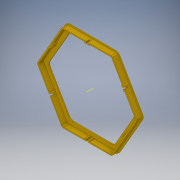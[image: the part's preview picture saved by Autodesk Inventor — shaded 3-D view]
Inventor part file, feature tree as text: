
AUTODESK INVENTOR PART (.ipt)
format: ipt  version: 2019 (Build 230136000, 136)  size: 541,696 bytes
history: native  units: mm
features: extrude x5, sketch x5, projected_geometry x3, fillet x2, other x1, pattern_circular x1
ambient origin geometry x8: Origin, YZ Plane, XZ Plane, XY Plane, X Axis, Y Axis, Z Axis, Center Point
bodies: Solid1 (feature_tree)
feature tree (17):
  extrude  "Extrusion1"  Depth=2.0mm
  extrude  "Extrusion5"  Depth=2.0mm
  extrude  "Extrusion6"  Depth=10.0mm
  fillet  "Fillet1"  [1 undecoded]
  fillet  "Fillet2"  Radius=8.0mm
  extrude  "Extrusion7"  TaperAngle=0.0deg  [1 undecoded]
  extrude  "Extrusion8"  Depth=4.0mm
  other  "Work Axis2"
  pattern_circular  "Circular Pattern1"  [2 undecoded]
  sketch  "Sketch1"  dims[d0=175.0mm d1=2.0mm]
  sketch  "Sketch5"  dims[d2=0.0mm d15=2.0mm]
  projected_geometry  "Projected Loop4"
  sketch  "Sketch7"  dims[d16=2.0mm d17=10.0mm d18=0.0mm d19=8.0mm]
  projected_geometry  "Projected Loop6"
  sketch  "Sketch8"  dims[d20=7.0mm d21=0.0mm]
  sketch  "Sketch9"  dims[d22=10.0mm d23=4.0mm d24=10.0mm d25=3.3mm d26=6.5mm d27=0.0mm d28=4.0mm d29=3.0mm d30=5.0mm d31=0.0mm d32=60.0mm d33=360.0deg]
  projected_geometry  "Projected Loop7"
note: 4 required parameter values undecoded (feature->parameter linkage not recoverable at this tier; creation-order binding heuristic only, values carry confidence <= 0.55)
